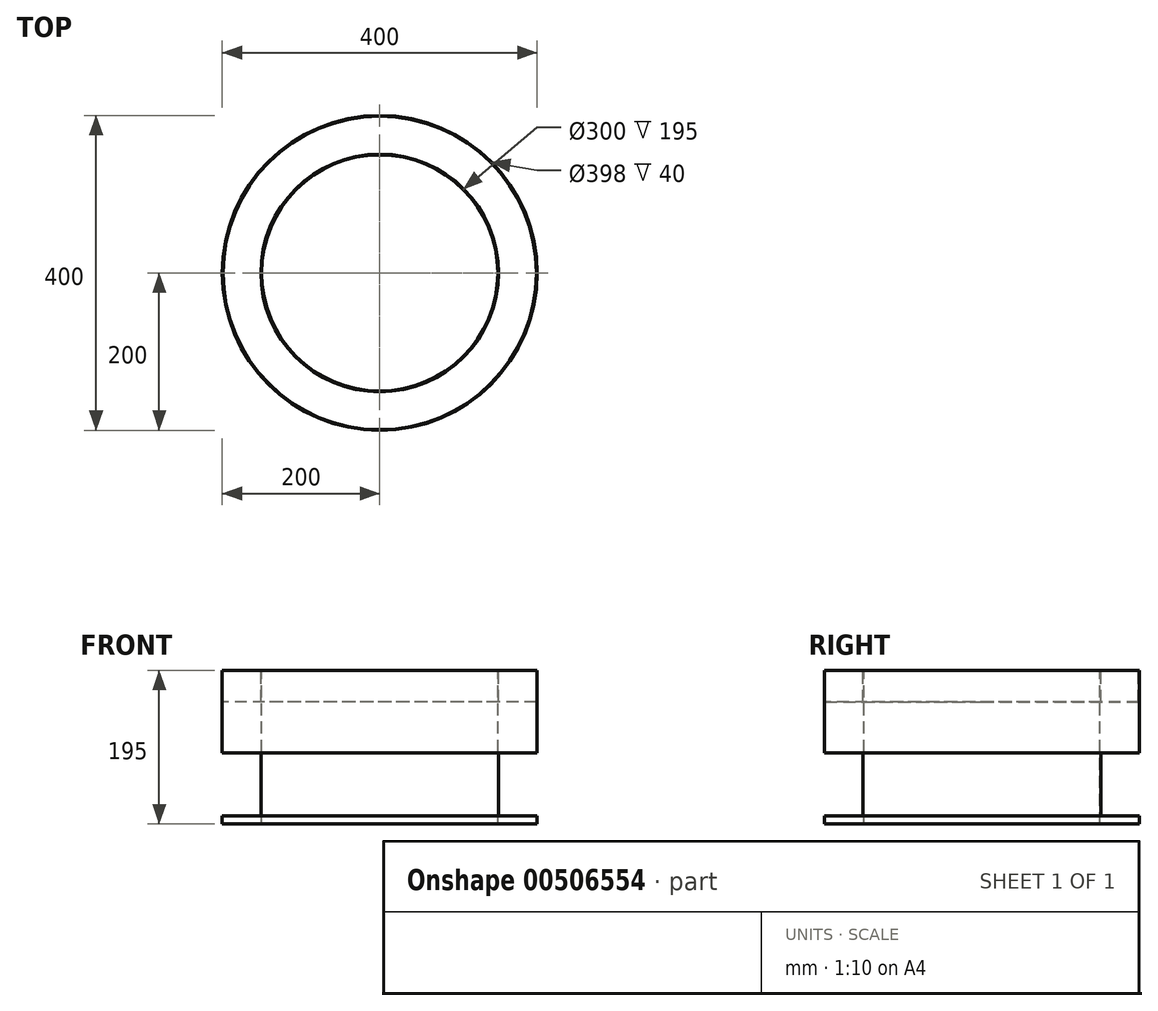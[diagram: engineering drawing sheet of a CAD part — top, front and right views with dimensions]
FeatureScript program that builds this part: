
annotation { "Feature Type Name" : "Feature", "Feature Type Description" : "" }
export const myFeature = defineFeature(function(context is Context, id is Id, definition is map)
    precondition{}
    {
        {
            var Q0;
            Q0=qCreatedBy(makeId("Front.planeOp"),FACE);
            var sketch = newSketch(context, id + "F0", { "sketchPlane" : qUnion([Q0])});
            skLineSegment(sketch, "E0", {"start": v(0, 710.75) * mm, "end": v(0, -704.58) * mm, "construction": true});
            skLineSegment(sketch, "E1", {"start": v(-150, 300.65) * mm, "end": v(-150, 495.65) * mm});
            skLineSegment(sketch, "E2", {"start": v(-150, 495.65) * mm, "end": v(-151, 495.65) * mm});
            skLineSegment(sketch, "E3", {"start": v(-199, 495.65) * mm, "end": v(-200, 495.65) * mm});
            skLineSegment(sketch, "E4", {"start": v(-200, 495.65) * mm, "end": v(-200, 390.65) * mm});
            skLineSegment(sketch, "E5", {"start": v(-200, 390.65) * mm, "end": v(-151, 390.65) * mm});
            skLineSegment(sketch, "E6", {"start": v(-151, 390.65) * mm, "end": v(-151, 310.65) * mm});
            skLineSegment(sketch, "E7", {"start": v(-151, 310.65) * mm, "end": v(-200, 310.65) * mm});
            skLineSegment(sketch, "E8", {"start": v(-200, 310.65) * mm, "end": v(-200, 300.65) * mm});
            skLineSegment(sketch, "E9", {"start": v(-200, 300.65) * mm, "end": v(-150, 300.65) * mm});
            skLineSegment(sketch, "E10", {"start": v(-199, 495.65) * mm, "end": v(-199, 455.65) * mm});
            skLineSegment(sketch, "E11", {"start": v(-199, 455.65) * mm, "end": v(-151, 455.65) * mm});
            skLineSegment(sketch, "E12", {"start": v(-151, 455.65) * mm, "end": v(-151, 495.65) * mm});
            skSolve(sketch);
        }
        {
            var Q0;
            Q0=qSketchRegion(id+"F0",true);
            var Q1;
            Q1=sQuery(id+"F0.wireOp",EDGE,"E0");
            revolve(context, id + "F1", {"entities" : qUnion([Q0]), "axis" : qUnion([Q1]), "revolveType" : RevolveType.FULL});
        }
    });
